# Revit family: WAGNER_Фильтр_специальный_Typ_SF_650
name_source: partatom
category: Оборудование
revit_build: Autodesk Revit 2017 (Build: 20190508_0315(x64)
units: mm (PartAtom-declared; Revit-internal decimal feet)

## family parameters
Всегда вертикально = Да
Заголовок OmniClass = Dust Collectors
На основе рабочей плоскости = Нет
Номер OmniClass = 23.70.30.24.17
Общий = Да
При загрузке вырезать с полостями = Нет
Размер круглого соединителя = Использовать диаметр
Тип детали = Нормальный
Точка расчета площади = Нет

## types (1)
- Typ SF-650
    ADSK_URL документации изделия = https://ru.wagnergroup.com
    ADSK_URL страницы изделия = https://ru.wagnergroup.com
    ADSK_Версия Revit = Revit 2017
    ADSK_Версия семейства = Версия 1
    ADSK_Дата изменения = 18.07.20
    ADSK_Единица измерения = шт.
    ADSK_Завод-изготовитель = WAGNER
    ADSK_Код изделия = -
    ADSK_Марка = Typ SF-650
    ADSK_Материал = WAGNER_Фильтр_специальный
    ADSK_Наименование = Фильтр специальный Typ SF-650
    ADSK_Наименование краткое = Фильтр специальный
    ADSK_Размер_Высота = 0 мм
    ADSK_Размер_Длина = 0 мм
    ADSK_Размер_Ширина = 0 мм
    COBie Category = Air filters
    Masterformat Code = 23 01 30.51
    Masterformat Title = HVAC Air-Distribution System Cleaning
    OmniClass Code = 23-27 57 27
    OmniClass Title = Air Filters
    UNSPSC Code = 401615
    UNSPSC Title = Filters
    URL = www.wagner-russia.com
    Uniclass Code = Pr_65_57_02
    Uniclass Title = Air filters
    WAGNER_Variation = 1
    WAGNER_Артикул = AD-10-2000
    WAGNER_Название = Фильтр специальный Typ SF-650
    WAGNER_Температурный режим. = от -20℃ до +60℃
    WAGNER_Тип = Typ SF-650
    bimon.ru = bimon.ru
    Изготовитель = WAGNER
    Описание = Фильтр специальный Typ SF-650
